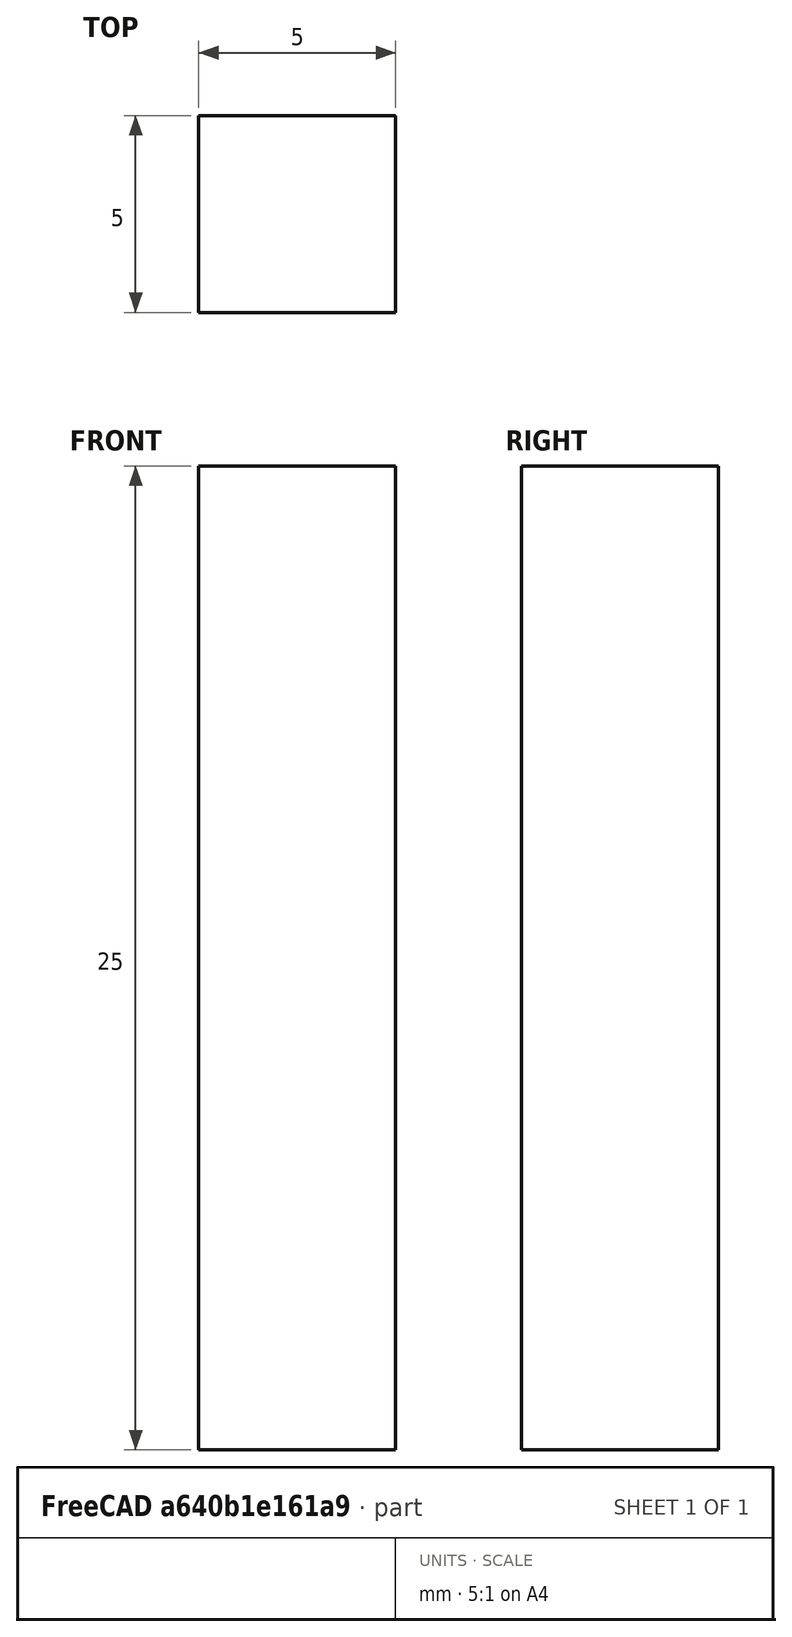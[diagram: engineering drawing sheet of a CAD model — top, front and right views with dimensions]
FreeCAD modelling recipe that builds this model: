
FCSTD DOCUMENT  (FreeCAD 0.16R)
Label: CatanRoad
License: All rights reserved
LicenseURL: http://en.wikipedia.org/wiki/All_rights_reserved
objects: Sketcher::SketchObject×1, PartDesign::Pad×1
note: 3 computed .brp shape members not serialized (recipe doc carries the construction recipe); baked Part::Feature solids carry a one-line shape summary decoded from their .brp

FEATURE [Sketcher::SketchObject] Sketch
  sketch-geometry (4):
    g0: LineSegment StartX=2.5 StartY=2.5 StartZ=0 EndX=-2.5 EndY=2.5 EndZ=0
    g1: LineSegment StartX=-2.5 StartY=2.5 StartZ=0 EndX=-2.5 EndY=-2.5 EndZ=0
    g2: LineSegment StartX=-2.5 StartY=-2.5 StartZ=0 EndX=2.5 EndY=-2.5 EndZ=0
    g3: LineSegment StartX=2.5 StartY=-2.5 StartZ=0 EndX=2.5 EndY=2.5 EndZ=0
  constraints (11):
    c: Coincident(g0,g1)
    c: Coincident(g1,g2)
    c: Coincident(g2,g3)
    c: Coincident(g3,g0)
    c: Horizontal(g0)
    c: Horizontal(g2)
    c: Vertical(g1)
    c: Vertical(g3)
    c: Symmetric(g1,g0,g-1)
    c: Equal(g0,g1)
    c: Distance(g0) = 5
FEATURE [PartDesign::Pad] Pad
  Length = 25
  Length2 = 100
  Sketch = -> Sketch
  Type = 0
